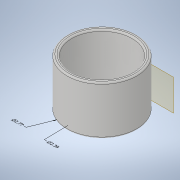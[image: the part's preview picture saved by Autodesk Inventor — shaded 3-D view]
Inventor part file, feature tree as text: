
AUTODESK INVENTOR PART (.ipt)
format: ipt  version: 2021.1 (Build 251245010, 245A)  size: 817,152 bytes
history: native  units: in
note: dims shown in document units (in); Inventor stores cm internally (conversion verified against a paired STEP export)
features: other x3, extrude x2, fillet x2, sketch x2, plane x1, emboss x1
ambient origin geometry x8: Origin, YZ Plane, XZ Plane, XY Plane, X Axis, Y Axis, Z Axis, Center Point
bodies: Solid1 (feature_tree)
feature tree (11):
  other  "Annotations"
  extrude  "Extrusion1"  Depth=0.1875in
  extrude  "Extrusion3"  Depth=0.0625in
  plane  "Work Plane1"
  emboss  "Emboss1"
  fillet  "Fillet1"  Radius=2.765in
  fillet  "Fillet2"  Radius=1.75in
  sketch  "Sketch1"  dims[d0=2.765in d2=0.1875in]
  sketch  "Sketch5"  dims[d3=0.0in d4=2.39in d5=2.765in d9=1.75in d10=0.0in d11=0.05in d12=0.0in d13=0.0625in d14=0.0625in d15=0.6263in d16=2.39in d17=0.7691in d18=2.765in]
  other  "Diameter Dimension 1"
  other  "Diameter Dimension 2"
